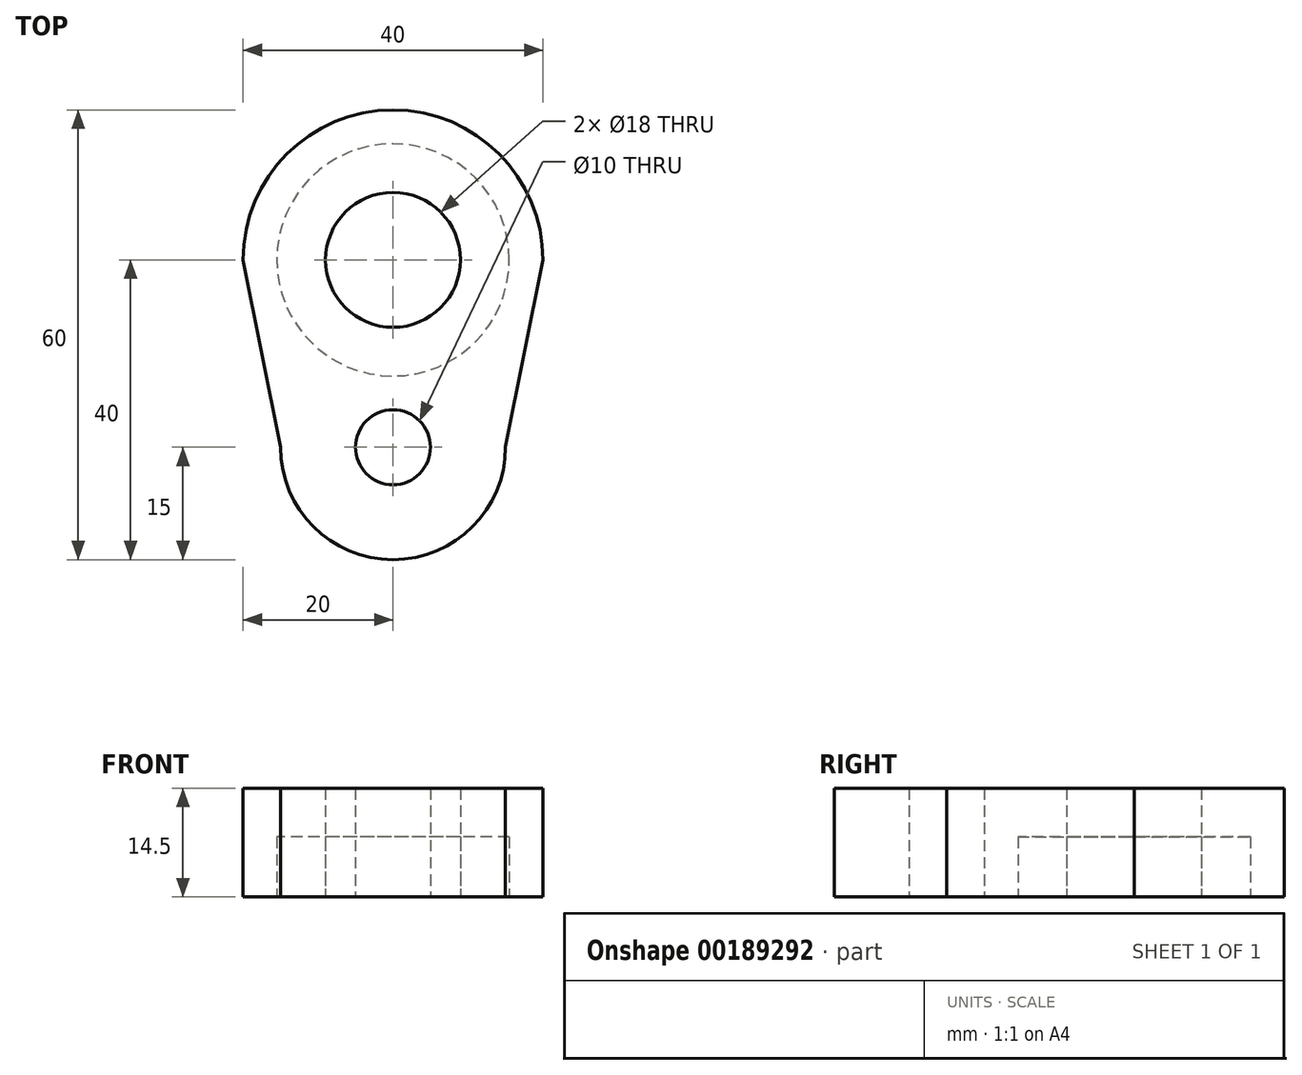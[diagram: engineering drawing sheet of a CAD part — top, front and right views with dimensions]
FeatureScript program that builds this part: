
annotation { "Feature Type Name" : "Feature", "Feature Type Description" : "" }
export const myFeature = defineFeature(function(context is Context, id is Id, definition is map)
    precondition{}
    {
        {
            var Q0;
            Q0=qCreatedBy(makeId("Top.planeOp"),FACE);
            var sketch = newSketch(context, id + "F0", { "sketchPlane" : qUnion([Q0])});
            skCircle(sketch, "E0", {"center": v(0, 25) * mm, "radius": 9 * mm});
            skCircle(sketch, "E1", {"center": v(0, 0) * mm, "radius": 5 * mm});
            skPoint(sketch, "E2", {"position": v(0, 5) * mm});
            skPoint(sketch, "E3", {"position": v(0, 16) * mm});
            skArc(sketch, "E4", {"start": v(20, 25) * mm, "mid": v(0, 45) * mm, "end": v(-20, 25) * mm});
            skArc(sketch, "E5", {"start": v(-15, 0) * mm, "mid": v(0, -15) * mm, "end": v(15, 0) * mm});
            skLineSegment(sketch, "E6", {"start": v(33.43, 25) * mm, "end": v(-32.2, 25) * mm, "construction": true});
            skLineSegment(sketch, "E7", {"start": v(34.41, 0) * mm, "end": v(-33.67, 0) * mm, "construction": true});
            skPoint(sketch, "E8", {"position": v(-20, 25) * mm});
            skPoint(sketch, "E9", {"position": v(20, 25) * mm});
            skPoint(sketch, "E10", {"position": v(15, 0) * mm});
            skPoint(sketch, "E11", {"position": v(-15, 0) * mm});
            skLineSegment(sketch, "E12", {"start": v(-20, 25) * mm, "end": v(-15, 0) * mm});
            skLineSegment(sketch, "E13", {"start": v(20, 25) * mm, "end": v(15, 0) * mm});
            skSolve(sketch);
        }
        {
            var Q0;
            Q0=makeQuery(id+"F0.imprint","IMPRINT",FACE,{"disambiguationData":[TD([[makeQuery(id+"F0.imprint","IMPRINT",EDGE,{"derivedFrom":sQuery(id+"F0.wireOp",EDGE,"E0")}),-1.0]])]});
            extrude(context, id + "F1", {"entities" : qUnion([Q0]), "depth" : 14.5 * mm});
        }
        {
            var Q0;
            Q0=qCreatedBy(makeId("Top.planeOp"),FACE);
            var sketch = newSketch(context, id + "F2", { "sketchPlane" : qUnion([Q0])});
            skCircle(sketch, "E14", {"center": v(0, 25) * mm, "radius": 9 * mm});
            skCircle(sketch, "E15", {"center": v(0, 25) * mm, "radius": 15.5 * mm});
            skSolve(sketch);
        }
        {
            var Q0;
            Q0=makeQuery(id+"F2.imprint","IMPRINT",FACE,{"disambiguationData":[TD([[makeQuery(id+"F2.imprint","IMPRINT",EDGE,{"derivedFrom":sQuery(id+"F2.wireOp",EDGE,"E14")}),-1.0]])]});
            extrude(context, id + "F3", {"entities" : qUnion([Q0]), "depth" : 8 * mm});
        }
    });
